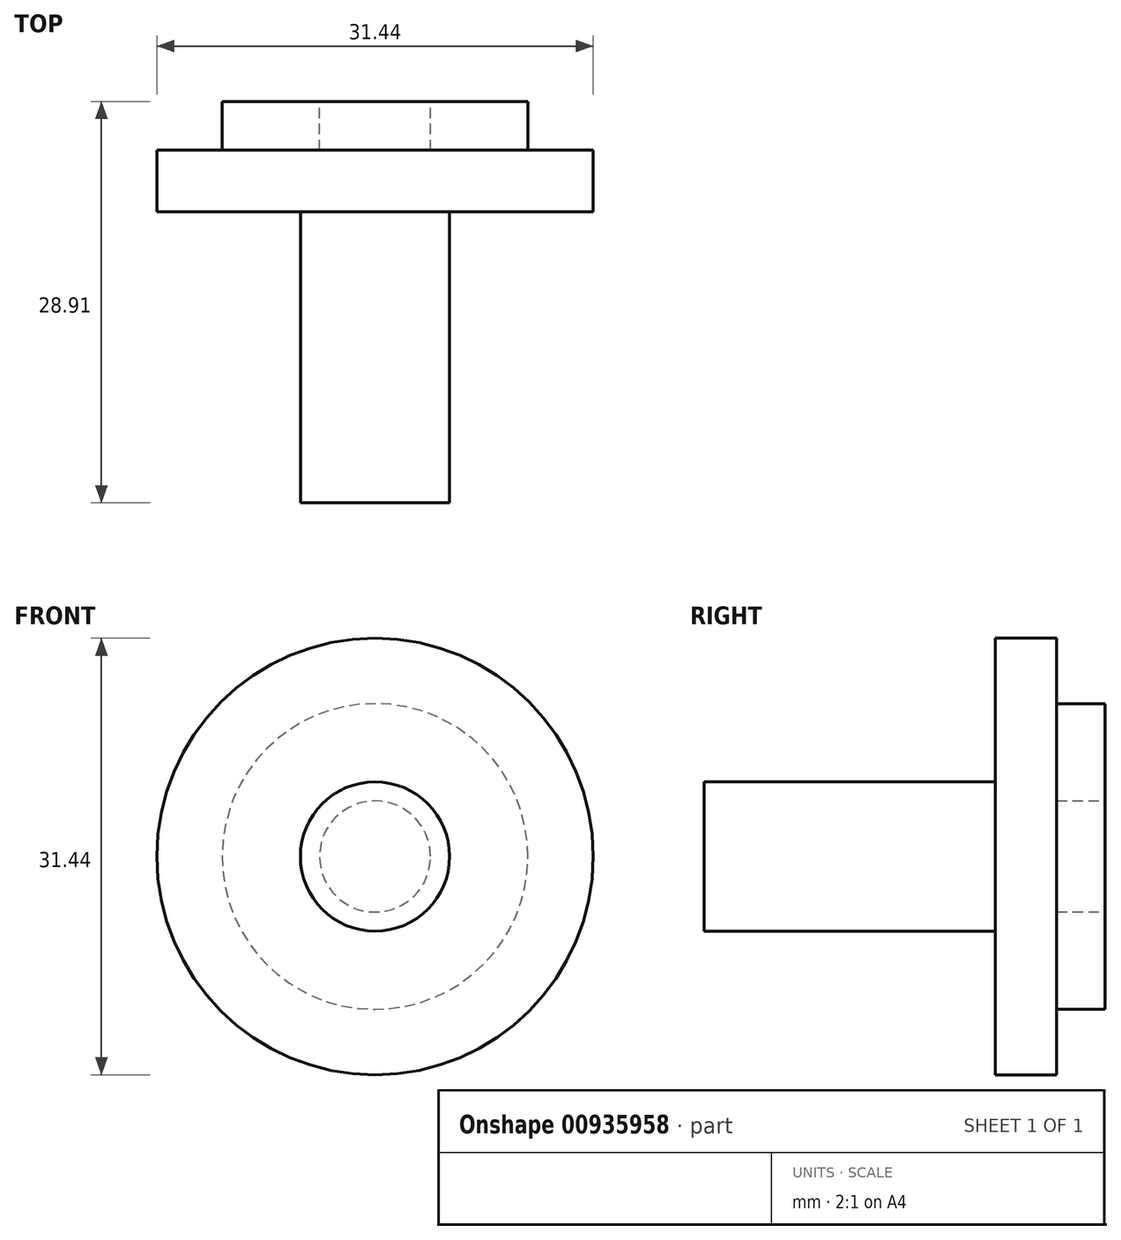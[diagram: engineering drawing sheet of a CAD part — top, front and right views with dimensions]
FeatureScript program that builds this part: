
annotation { "Feature Type Name" : "Feature", "Feature Type Description" : "" }
export const myFeature = defineFeature(function(context is Context, id is Id, definition is map)
    precondition{}
    {
        {
            var Q0;
            Q0=qCreatedBy(makeId("Front.planeOp"),FACE);
            var sketch = newSketch(context, id + "F0", { "sketchPlane" : qUnion([Q0])});
            skCircle(sketch, "E0", {"center": v(0, 0) * mm, "radius": 11.01 * mm});
            skCircle(sketch, "E1", {"center": v(0, 0) * mm, "radius": 4 * mm});
            skSolve(sketch);
        }
        {
            var Q0;
            Q0=makeQuery(id+"F0.imprint","IMPRINT",FACE,{"disambiguationData":[TD([[makeQuery(id+"F0.imprint","IMPRINT",EDGE,{"derivedFrom":sQuery(id+"F0.wireOp",EDGE,"E0")}),1.0]])]});
            extrude(context, id + "F1", {"entities" : qUnion([Q0]), "depth" : 7 * mm, "offsetDistance" : 25.4 * mm, "symmetric" : true});
        }
        {
            var Q0;
            Q0=qCreatedBy(makeId("Front.planeOp"),FACE);
            var sketch = newSketch(context, id + "F2", { "sketchPlane" : qUnion([Q0])});
            skCircle(sketch, "E2", {"center": v(0, 0) * mm, "radius": 15.72 * mm});
            skSolve(sketch);
        }
        {
            var Q0;
            Q0=makeQuery(id+"F2.imprint","IMPRINT",FACE,{"disambiguationData":[TD([[makeQuery(id+"F2.imprint","IMPRINT",EDGE,{"derivedFrom":sQuery(id+"F2.wireOp",EDGE,"E2")}),1.0]])]});
            extrude(context, id + "F3", {"entities" : qUnion([Q0]), "operationType" : NewBodyOperationType.ADD, "depth" : 4.43 * mm, "offsetDistance" : 25.4 * mm});
        }
        {
            var Q0;
            Q0=qCreatedBy(makeId("Front.planeOp"),FACE);
            var sketch = newSketch(context, id + "F4", { "sketchPlane" : qUnion([Q0])});
            skCircle(sketch, "E3", {"center": v(0, 0) * mm, "radius": 5.38 * mm});
            skSolve(sketch);
        }
        {
            var Q0;
            Q0=makeQuery(id+"F4.imprint","IMPRINT",FACE,{"disambiguationData":[TD([[makeQuery(id+"F4.imprint","IMPRINT",EDGE,{"derivedFrom":sQuery(id+"F4.wireOp",EDGE,"E3")}),1.0]])]});
            extrude(context, id + "F5", {"entities" : qUnion([Q0]), "operationType" : NewBodyOperationType.ADD, "depth" : 25.4 * mm, "offsetDistance" : 25.4 * mm});
        }
    });
